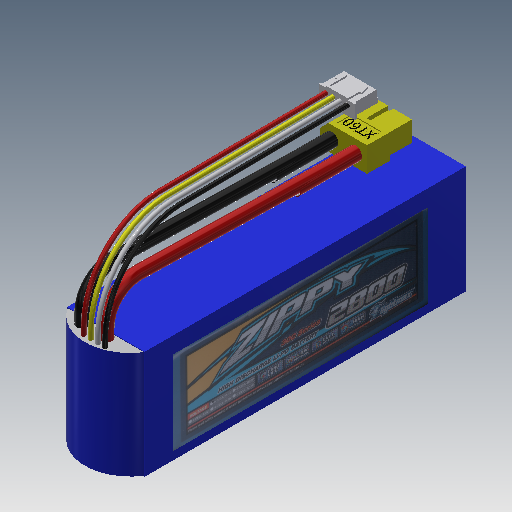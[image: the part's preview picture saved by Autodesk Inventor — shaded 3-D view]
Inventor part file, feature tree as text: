
AUTODESK INVENTOR PART (.ipt)
format: ipt  version: 2018 (Build 220112000, 112)  size: 2,228,224 bytes
history: native  units: mm
features: sketch x30, extrude x23, plane x4, pattern_linear x3, sweep x3, fillet x2, other x2, emboss x1, projected_geometry x1
ambient origin geometry x8: Origin, YZ Plane, XZ Plane, XY Plane, X Axis, Y Axis, Z Axis, Center Point
bodies: Solid1 (feature_tree)
feature tree (69):
  extrude  "Extrusion1"  Depth=35.0mm
  extrude  "Extrusion2"  Depth=2.0mm
  pattern_linear  "Rectangular Pattern1"  Count1=2 Spacing1=9.333333mm
  fillet  "Fillet1"  Radius=2.0mm
  extrude  "Extrusion3"  Depth=105.0mm TaperAngle=0.0deg
  plane  "Work Plane1"
  extrude  "Extrusion4"  Depth=13.8mm
  extrude  "Extrusion5"  Depth=11.6mm
  extrude  "Extrusion6"  Depth=30.0mm
  extrude  "Extrusion7"  Depth=7.85mm TaperAngle=0.0deg
  extrude  "Extrusion8"  Depth=4.0mm
  extrude  "Extrusion9"  Depth=1.8mm
  plane  "Work Plane2"
  emboss  "Emboss1"
  extrude  "Extrusion10"  Depth=0.75mm
  extrude  "Extrusion11"  Depth=7.6mm TaperAngle=0.0deg
  sketch  "Sketch13"  dims[d32=1.0mm d33=0.0mm d34=1.8mm]
  sketch  "3D Sketch1"
  sweep  "Sweep1"
  sweep  "Sweep2"
  extrude  "Extrusion12"  Depth=60.0mm
  plane  "Work Plane3"
  extrude  "Extrusion13"  Depth=10.0mm TaperAngle=0.0deg
  extrude  "Extrusion14"  Depth=4.3mm
  extrude  "Extrusion15"  Depth=0.3mm TaperAngle=0.0deg
  extrude  "Extrusion16"  Depth=3.5mm
  extrude  "Extrusion17"  Depth=4.0mm
  extrude  "Extrusion18"  Depth=3.9mm
  extrude  "Extrusion19"  Depth=7.8mm
  extrude  "Extrusion20"  Depth=10.0mm
  extrude  "Extrusion21"  Depth=10.0mm
  pattern_linear  "Rectangular Pattern2"  Spacing1=0.0mm  [1 undecoded]
  sketch  "Sketch25"  dims[d74=0.3mm d75=0.0mm d76=3.9mm]
  sweep  "Sweep3"
  pattern_linear  "Rectangular Pattern3"  Spacing1=10.337mm  [1 undecoded]
  extrude  "Extrusion22"  Depth=20.0mm TaperAngle=0.0deg
  plane  "Work Plane4"
  extrude  "Extrusion23"  [1 undecoded]
  fillet  "Fillet4"  Radius=10.6mm
  other  "Decal1"
  sketch  "Sketch1"  dims[d0=25.0mm d1=35.0mm]
  sketch  "Sketch2"  dims[d2=105.0mm d3=0.0mm d4=2.0mm]
  sketch  "Sketch3"  dims[d5=2.0mm]
  sketch  "Sketch4"  dims[d6=25.0mm]
  sketch  "Sketch5"  dims[d7=8.333333mm]
  sketch  "Sketch6"  dims[d8=105.0mm d9=0.0mm d10=20.0mm d12=9.333333mm d13=2.0mm]
  sketch  "Sketch7"  dims[d14=8.0mm d15=105.0mm d16=0.0mm]
  sketch  "Sketch8"  dims[d17=-10.0mm d18=13.8mm]
  sketch  "Sketch9"  dims[d19=6.6mm d20=11.6mm]
  sketch  "Sketch10"  dims[d21=2.2mm d22=30.0mm]
  sketch  "Sketch11"  dims[d26=6.6mm d27=7.85mm d28=0.0mm]
  sketch  "Sketch12"  dims[d29=1.0mm d30=4.0mm]
  sketch  "Sketch14"  dims[d35=1.0mm d36=0.0mm d37=0.75mm]
  sketch  "Sketch15"  dims[d38=0.75mm d39=7.6mm d40=0.0mm]
  sketch  "Sketch16"  dims[d41=10.0mm d42=0.3mm d43=0.0mm]
  sketch  "Sketch17"  dims[d44=0.1mm d45=4.93934mm]
  sketch  "Sketch18"  dims[d46=0.70562mm d54=60.0mm d56=0.70562mm]
  sketch  "Sketch19"  dims[d57=10.0mm d59=10.0mm d61=0.3mm d62=0.0mm]
  sketch  "Sketch20"  dims[d63=1.0mm d64=0.0mm d65=4.3mm]
  sketch  "Sketch21"  dims[d67=3.4mm d68=0.3mm d69=0.0mm]
  sketch  "Sketch22"  dims[d70=3.5mm d71=3.5mm]
  sketch  "Sketch24"  dims[d72=4.0mm d73=4.0mm]
  sketch  "Sketch26"  dims[d77=3.9mm d78=7.8mm]
  sketch  "3D Sketch2"
  sketch  "Sketch27"  dims[d80=10.0mm d81=13.5mm]
  projected_geometry  "Projected Loop1"
  sketch  "Sketch29"  dims[d82=13.5mm d83=10.0mm]
  sketch  "Sketch31"  dims[d84=10.0mm d85=0.0mm d86=0.0mm d87=10.337mm d88=20.0mm d89=0.0mm d90=-10.0mm d91=10.6mm d92=3.9mm d93=42.0mm d94=7.7mm d95=0.0mm d96=5.0mm d97=0.7mm d98=0.0mm d99=1.25mm d100=0.5mm d101=5.8mm d102=2.6mm d103=2.2mm d104=0.5mm d105=0.7mm d106=0.0mm d107=0.7mm d108=0.0mm d109=1.1mm d110=1.1mm d111=0.85mm d112=10.6mm d113=1.79mm d114=40.0mm d116=2.34mm d117=10.0mm d119=10.0mm d121=0.7mm d122=0.0mm d123=3.0mm d124=3.0mm d125=0.0mm d126=1.5mm d127=0.5mm d128=0.0mm d129=0.05mm d130=0.05mm d131=0.5mm d132=0.0mm d136=0.05mm d137=0.05mm d138=0.05mm d139=0.5mm d140=0.0mm d141=40.0mm d143=2.34mm d144=1.4mm d145=1.4mm d146=10.253mm d147=5.0mm d148=28.0mm d149=25.0mm d150=0.0mm d151=40.0mm d153=2.34mm d154=0.2mm d155=0.5mm d156=0.0mm d157=0.1mm d158=10.0mm d159=13.0mm d160=0.1mm d161=0.0mm d166=2.0mm d174=0.0mm d175=0.0mm d176=0.0mm]
  other  "Image1"
note: 3 required parameter values undecoded (feature->parameter linkage not recoverable at this tier; creation-order binding heuristic only, values carry confidence <= 0.55)
